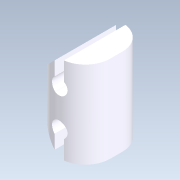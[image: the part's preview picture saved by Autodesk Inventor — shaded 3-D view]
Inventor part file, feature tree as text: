
AUTODESK INVENTOR PART (.ipt)
format: ipt  version: 2020.2 (Build 242310000, 310)  size: 163,328 bytes
history: native  units: mm
features: extrude x3, sketch x3, fillet x1
ambient origin geometry x8: Origin, YZ Plane, XZ Plane, XY Plane, X Axis, Y Axis, Z Axis, Center Point
bodies: Solid1 (feature_tree)
feature tree (7):
  extrude  "Extrusion1"  Depth=28.0mm
  extrude  "Extrusion2"  Depth=17.0mm
  fillet  "Fillet1"  Radius=17.0mm
  extrude  "Extrusion4"  TaperAngle=0.0deg  [1 undecoded]
  sketch  "Sketch1"  dims[d1=2.5mm d2=28.0mm]
  sketch  "Sketch2"  dims[d3=5.0mm d5=17.0mm d9=17.0mm]
  sketch  "Sketch4"  dims[d10=2.5mm d11=0.0mm d12=135.0deg d13=135.0deg d14=20.0mm d15=0.0mm d16=8.0mm d17=5.0mm d18=1.5mm d19=3.0mm d20=8.0mm d21=1.5mm d22=1.5mm d23=5.0mm d24=0.0mm d25=0.0mm d26=8.0mm d31=2.0mm d32=2.0mm d33=0.0mm d34=0.0mm]
note: 1 required parameter value undecoded (feature->parameter linkage not recoverable at this tier; creation-order binding heuristic only, values carry confidence <= 0.55)
